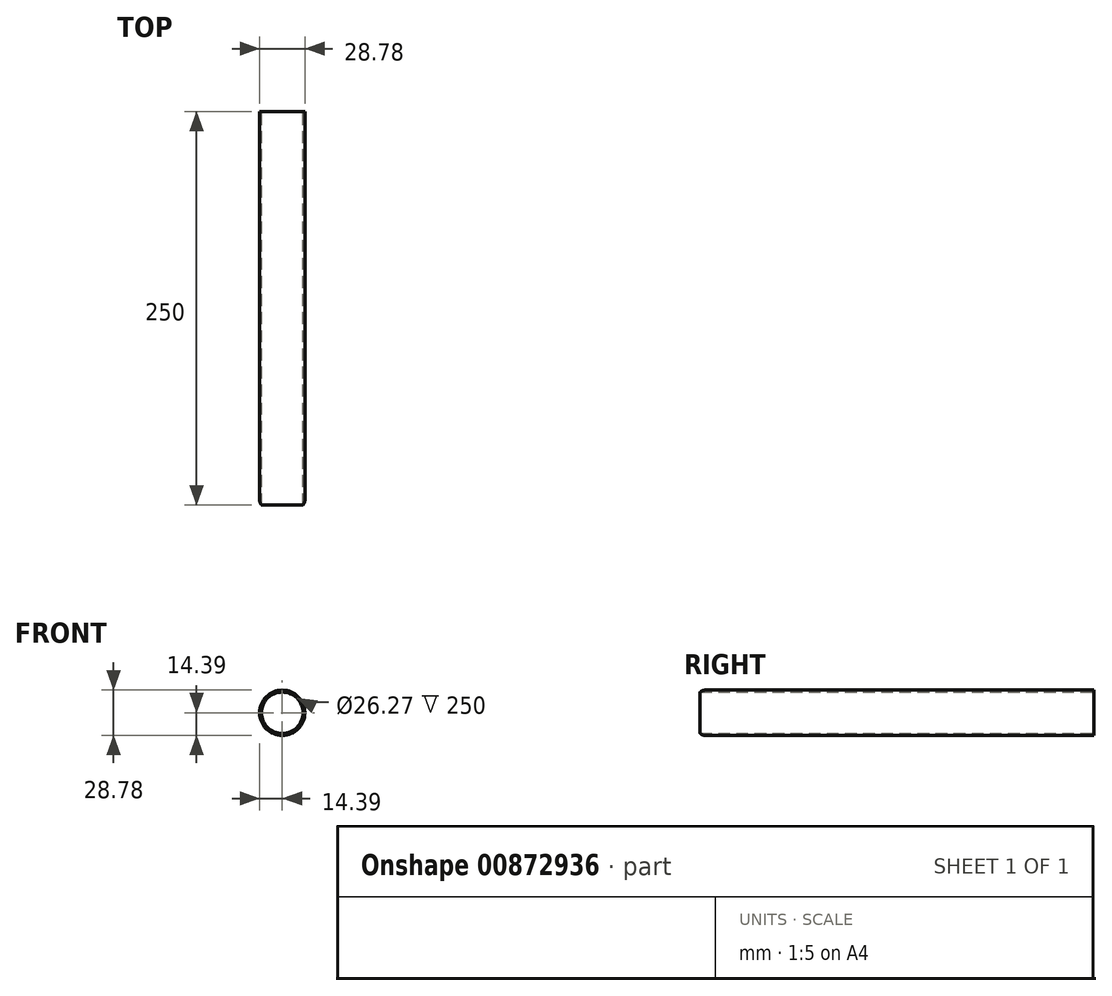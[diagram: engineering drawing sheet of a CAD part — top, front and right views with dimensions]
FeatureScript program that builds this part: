
annotation { "Feature Type Name" : "Feature", "Feature Type Description" : "" }
export const myFeature = defineFeature(function(context is Context, id is Id, definition is map)
    precondition{}
    {
        {
            var Q0;
            Q0=qCreatedBy(makeId("Front.planeOp"),FACE);
            var sketch = newSketch(context, id + "F0", { "sketchPlane" : qUnion([Q0])});
            skCircle(sketch, "E0", {"center": v(0, 0) * mm, "radius": 13.13 * mm});
            skCircle(sketch, "E1", {"center": v(0, 0) * mm, "radius": 14.4 * mm});
            skCircle(sketch, "E2", {"center": v(9.33, -9.25) * mm, "radius": 1.26 * mm});
            skSolve(sketch);
        }
        {
            var Q0;
            {var subQ4=sQuery(id+"F0.wireOp",EDGE,"E1");Q0=makeQuery(id+"F0.imprint","IMPRINT",FACE,{"disambiguationData":[TD([[makeQuery(id+"F0.imprint","IMPRINT",EDGE,{"derivedFrom":subQ4}),1.0]])]});}
            var Q1;
            Q1 = qSketchRegion(id + "F0", true);
            extrude(context, id + "F1", {"entities" : qUnion([Q0, Q1]), "depth" : 250 * mm, "offsetDistance" : 25 * mm});
        }
        {
            var Q0;
            Q0=makeQuery(id+"F1.opExtrude","CAP_EDGE",EDGE,{"disambiguationData":[OSD([sQuery(id+"F0.wireOp",EDGE,"E1")])],"isStart":false});
            fillet(context, id + "F2", {"entities" : qUnion([Q0]), "radius" : 5 * mm, "tangentPropagation" : true, "allowEdgeOverflow" : false});
        }
    });
